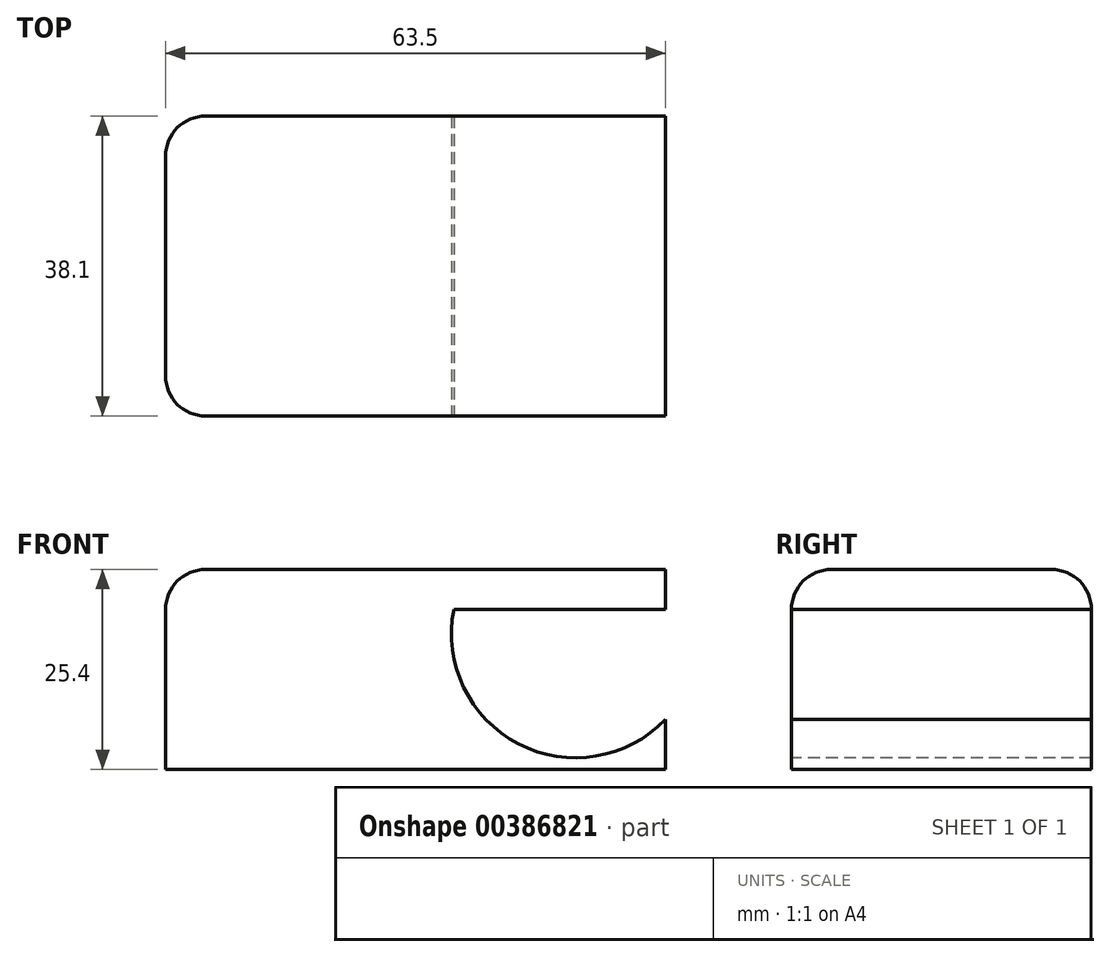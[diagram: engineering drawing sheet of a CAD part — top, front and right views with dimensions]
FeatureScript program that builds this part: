
annotation { "Feature Type Name" : "Feature", "Feature Type Description" : "" }
export const myFeature = defineFeature(function(context is Context, id is Id, definition is map)
    precondition{}
    {
        {
            var Q0;
            Q0=qCreatedBy(makeId("Top.planeOp"),FACE);
            var sketch = newSketch(context, id + "F0", { "sketchPlane" : qUnion([Q0])});
            skLineSegment(sketch, "E0", {"start": v(0, 0) * mm, "end": v(63.5, 0) * mm});
            skLineSegment(sketch, "E1", {"start": v(63.5, 0) * mm, "end": v(63.5, 38.1) * mm});
            skLineSegment(sketch, "E2", {"start": v(63.5, 38.1) * mm, "end": v(50.8, 38.1) * mm});
            skLineSegment(sketch, "E3", {"start": v(0, 0) * mm, "end": v(0, 38.1) * mm});
            skLineSegment(sketch, "E4", {"start": v(0, 38.1) * mm, "end": v(12.7, 38.1) * mm});
            skLineSegment(sketch, "E5", {"start": v(12.7, 38.1) * mm, "end": v(50.8, 38.1) * mm});
            skSolve(sketch);
        }
        {
            var Q0;
            Q0=makeQuery(id+"F0.imprint","IMPRINT",FACE,{"disambiguationData":[TD([[makeQuery(id+"F0.imprint","IMPRINT",EDGE,{"derivedFrom":sQuery(id+"F0.wireOp",EDGE,"E0")}),1.0]])]});
            extrude(context, id + "F1", {"entities" : qUnion([Q0]), "depth" : 25.4 * mm});
        }
        {
            var Q0;
            Q0=makeQuery(id+"F1.opExtrude","SWEPT_EDGE",EDGE,{"disambiguationData":[OSD([sQuery(id+"F0.wireOp",EDGE,"E0"),sQuery(id+"F0.wireOp",EDGE,"E3")])]});
            fillet(context, id + "F2", {"entities" : qUnion([Q0]), "radius" : 5.08 * mm, "tangentPropagation" : true, "allowEdgeOverflow" : false});
        }
        {
            var Q0;
            {var subQ0=sQuery(id+"F0.wireOp",EDGE,"E3");var subQ1=sQuery(id+"F0.wireOp",EDGE,"E0");Q0=makeQuery(id+"F2.opFillet","BLEND_EDGE",EDGE,{"blendedFrom":[makeQuery(id+"F1.opExtrude","SWEPT_EDGE",EDGE,{"disambiguationData":[OSD([subQ1,subQ0])]}),makeQuery(id+"F1.opExtrude","CAP_FACE",FACE,{"disambiguationData":[OSD([subQ1,sQuery(id+"F0.wireOp",EDGE,"E1"),sQuery(id+"F0.wireOp",EDGE,"E2"),subQ0,sQuery(id+"F0.wireOp",EDGE,"E4"),sQuery(id+"F0.wireOp",EDGE,"E5")])],"isStart":false})],"blendedInto":[makeQuery(id+"F1.opExtrude","CAP_FACE",FACE,{"disambiguationData":[OSD([subQ1,sQuery(id+"F0.wireOp",EDGE,"E1"),sQuery(id+"F0.wireOp",EDGE,"E2"),subQ0,sQuery(id+"F0.wireOp",EDGE,"E4"),sQuery(id+"F0.wireOp",EDGE,"E5")])],"isStart":false})]});}
            fillet(context, id + "F3", {"entities" : qUnion([Q0]), "radius" : 5.08 * mm, "tangentPropagation" : true, "allowEdgeOverflow" : false});
        }
        {
            var Q0;
            Q0=makeQuery(id+"F1.opExtrude","CAP_EDGE",EDGE,{"disambiguationData":[OSD([sQuery(id+"F0.wireOp",EDGE,"E2"),sQuery(id+"F0.wireOp",EDGE,"E4"),sQuery(id+"F0.wireOp",EDGE,"E5")])],"isStart":false});
            fillet(context, id + "F4", {"entities" : qUnion([Q0]), "radius" : 5.08 * mm, "tangentPropagation" : true, "allowEdgeOverflow" : false});
        }
        {
            var Q0;
            Q0=makeQuery(id+"F1.opExtrude","SWEPT_FACE",FACE,{"disambiguationData":[OSD([sQuery(id+"F0.wireOp",EDGE,"E0")])]});
            var sketch = newSketch(context, id + "F5", { "sketchPlane" : qUnion([Q0])});
            skArc(sketch, "E6", {"start": v(36.83, 21.3) * mm, "mid": v(44.38, 3.5) * mm, "end": v(63.5, 6.35) * mm});
            skSolve(sketch);
        }
        {
            var Q0;
            {var subQ0=sQuery(id+"F5.wireOp",EDGE,"E6");var subQ1=sQuery(id+"F0.wireOp",EDGE,"E0");var subQ2=makeQuery(id+"F1.opExtrude","SWEPT_EDGE",EDGE,{"disambiguationData":[OSD([subQ1,sQuery(id+"F0.wireOp",EDGE,"E1")])]});var subQ3=makeQuery(id+"F5.imprint","INTERSECT",VERTEX,{"derivedFrom":[subQ2,subQ0]});Q0=makeQuery(id+"F5.imprint","IMPRINT",FACE,{"disambiguationData":[TD([[makeQuery(id+"F5.imprint","IMPRINT",EDGE,{"disambiguationData":[TD([[subQ3,1.0]])],"derivedFrom":subQ0}),1.0]])]});}
            extrude(context, id + "F6", {"entities" : qUnion([Q0]), "operationType" : NewBodyOperationType.REMOVE, "oppositeDirection" : true, "depth" : 41.66 * mm});
        }
    });
